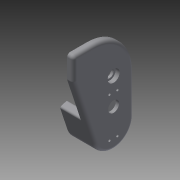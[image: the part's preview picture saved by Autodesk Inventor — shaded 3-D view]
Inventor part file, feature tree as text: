
AUTODESK INVENTOR PART (.ipt)
format: ipt  version: 2015 (Build 190159000, 159)  size: 267,776 bytes
history: native  units: mm
features: extrude x8, sketch x8, fillet x4
ambient origin geometry x8: Origin, YZ Plane, XZ Plane, XY Plane, X Axis, Y Axis, Z Axis, Center Point
bodies: Solid1 (feature_tree)
feature tree (20):
  extrude  "Extrusion1"  Depth=33.15mm
  extrude  "Extrusion2"  Depth=55.0mm
  extrude  "Extrusion3"  Depth=55.0mm
  extrude  "Extrusion4"  Depth=9.9mm
  extrude  "Extrusion5"  Depth=9.9mm
  extrude  "Extrusion6"  Depth=3.0mm
  extrude  "Extrusion7"  Depth=3.0mm
  fillet  "Fillet1"  Radius=3.0mm
  extrude  "Extrusion8"  Depth=25.0mm
  fillet  "Fillet2"  Radius=45.0mm
  fillet  "Fillet3"  Radius=15.0mm
  fillet  "Fillet4"  Radius=5.0mm
  sketch  "Sketch1"  dims[d0=33.15mm d2=66.3mm]
  sketch  "Sketch2"  dims[d4=18.1mm d5=55.0mm]
  sketch  "Sketch3"  dims[d6=20.0mm d7=55.0mm]
  sketch  "Sketch4"  dims[d8=40.2mm d9=9.9mm]
  sketch  "Sketch5"  dims[d10=9.5mm d11=9.9mm]
  sketch  "Sketch6"  dims[d12=9.5mm d13=3.0mm]
  sketch  "Sketch7"  dims[d14=3.0mm d15=3.0mm d16=3.0mm]
  sketch  "Sketch8"  dims[d17=13.6mm d20=25.0mm d21=45.0mm d22=15.0mm d23=5.0mm d24=0.0mm d25=5.0mm d26=0.0mm d27=25.0mm d28=28.0mm d29=5.0mm d30=0.0mm d31=3.0mm d32=0.0mm d33=40.5mm d34=20.0mm d35=3.0mm d36=0.0mm d37=1.0mm d38=0.0mm d39=10.0mm d40=3.0mm d41=0.0mm d42=1.0mm d43=54.0mm d44=10.0mm d45=10.0mm d46=25.9mm d47=0.0mm d48=4.0mm d49=2.0mm d50=4.0mm]
